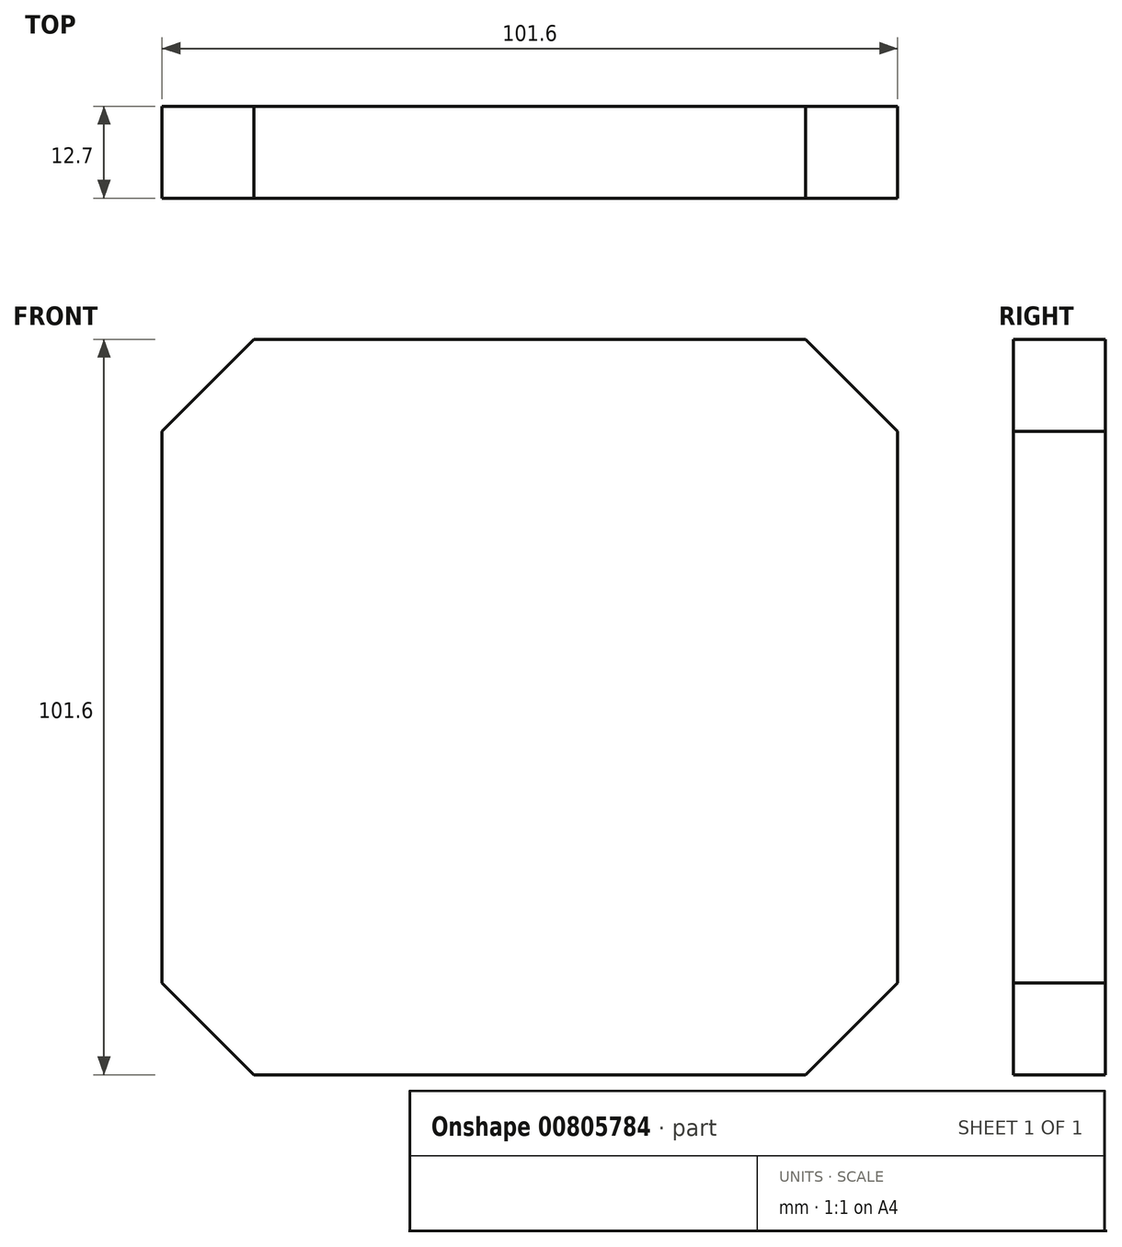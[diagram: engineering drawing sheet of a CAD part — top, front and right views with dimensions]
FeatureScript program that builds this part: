
annotation { "Feature Type Name" : "Feature", "Feature Type Description" : "" }
export const myFeature = defineFeature(function(context is Context, id is Id, definition is map)
    precondition{}
    {
        {
            var Q0;
            Q0=qCreatedBy(makeId("Front.planeOp"),FACE);
            var sketch = newSketch(context, id + "F0", { "sketchPlane" : qUnion([Q0])});
            skLineSegment(sketch, "E0.bottom", {"start": v(-50.8, 50.8) * mm, "end": v(50.8, 50.8) * mm});
            skLineSegment(sketch, "E0.top", {"start": v(-50.8, -50.8) * mm, "end": v(50.8, -50.8) * mm});
            skLineSegment(sketch, "E0.left", {"start": v(-50.8, 50.8) * mm, "end": v(-50.8, -50.8) * mm});
            skLineSegment(sketch, "E0.right", {"start": v(50.8, 50.8) * mm, "end": v(50.8, -50.8) * mm});
            skLineSegment(sketch, "E1", {"start": v(0, 50.8) * mm, "end": v(0, -50.8) * mm, "construction": true});
            skLineSegment(sketch, "E2", {"start": v(-50.8, 0) * mm, "end": v(50.8, 0) * mm, "construction": true});
            skSolve(sketch);
        }
        {
            var Q0;
            Q0=qSketchRegion(id+"F0",true);
            extrude(context, id + "F1", {"entities" : qUnion([Q0]), "depth" : 12.7 * mm, "offsetDistance" : 25.4 * mm});
        }
        {
            var Q0;
            Q0=makeQuery(id+"F1.opExtrude","SWEPT_EDGE",EDGE,{"disambiguationData":[OSD([sQuery(id+"F0.wireOp",EDGE,"E0.bottom"),sQuery(id+"F0.wireOp",EDGE,"E0.left")])]});
            var Q1;
            Q1=makeQuery(id+"F1.opExtrude","SWEPT_EDGE",EDGE,{"disambiguationData":[OSD([sQuery(id+"F0.wireOp",EDGE,"E0.bottom"),sQuery(id+"F0.wireOp",EDGE,"E0.right")])]});
            var Q2;
            Q2=makeQuery(id+"F1.opExtrude","SWEPT_EDGE",EDGE,{"disambiguationData":[OSD([sQuery(id+"F0.wireOp",EDGE,"E0.top"),sQuery(id+"F0.wireOp",EDGE,"E0.right")])]});
            var Q3;
            Q3=makeQuery(id+"F1.opExtrude","SWEPT_EDGE",EDGE,{"disambiguationData":[OSD([sQuery(id+"F0.wireOp",EDGE,"E0.top"),sQuery(id+"F0.wireOp",EDGE,"E0.left")])]});
            chamfer(context, id + "F2", {"entities" : qUnion([Q0, Q1, Q2, Q3]), "width" : 12.7 * mm, "tangentPropagation" : true});
        }
    });
